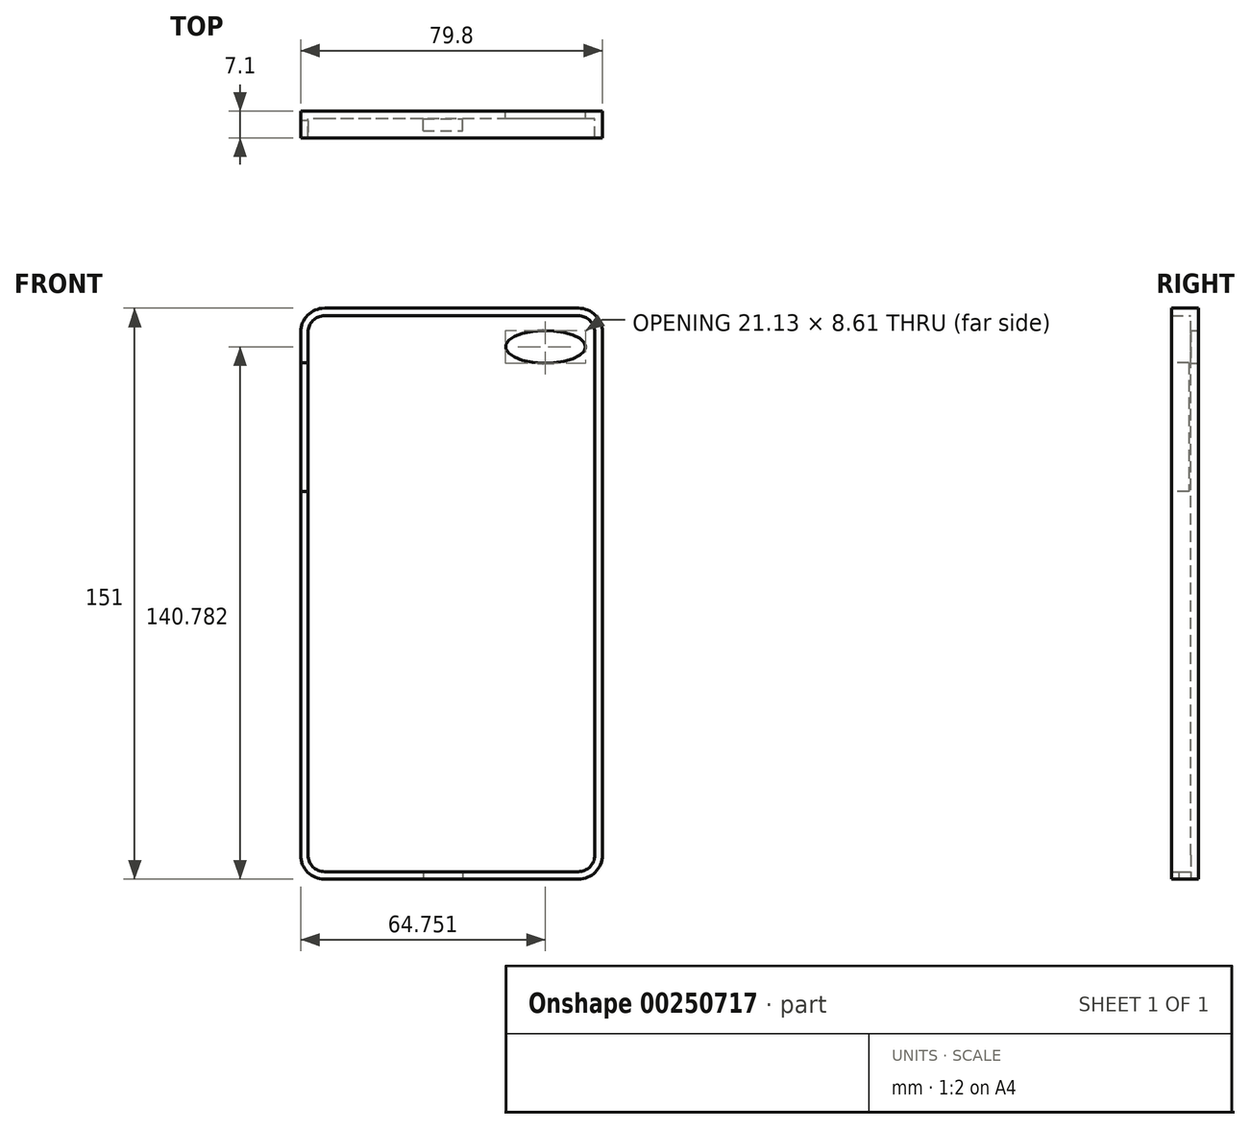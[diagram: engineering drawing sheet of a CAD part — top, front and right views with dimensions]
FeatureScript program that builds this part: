
annotation { "Feature Type Name" : "Feature", "Feature Type Description" : "" }
export const myFeature = defineFeature(function(context is Context, id is Id, definition is map)
    precondition{}
    {
        {
            var Q0;
            Q0=qCreatedBy(makeId("Front.planeOp"),FACE);
            var sketch = newSketch(context, id + "F0", { "sketchPlane" : qUnion([Q0])});
            skLineSegment(sketch, "E0.bottom", {"start": v(35.05, 79.1) * mm, "end": v(-32.05, 79.1) * mm});
            skLineSegment(sketch, "E0.top", {"start": v(35.05, -71.9) * mm, "end": v(-32.05, -71.9) * mm});
            skLineSegment(sketch, "E0.left", {"start": v(-38.4, -65.56) * mm, "end": v(-38.4, 72.74) * mm});
            skLineSegment(sketch, "E0.right", {"start": v(41.4, -65.56) * mm, "end": v(41.4, 72.74) * mm});
            skPoint(sketch, "E0.middle", {"position": v(1.5, 3.6) * mm});
            skLineSegment(sketch, "E1.bottom", {"start": v(27.8, -50.28) * mm, "end": v(-24, -50.28) * mm});
            skLineSegment(sketch, "E1.top", {"start": v(27.8, 61.47) * mm, "end": v(-24, 61.47) * mm});
            skLineSegment(sketch, "E1.left", {"start": v(27.8, -50.28) * mm, "end": v(27.8, 61.47) * mm});
            skLineSegment(sketch, "E1.right", {"start": v(-24, -50.28) * mm, "end": v(-24, 61.47) * mm});
            skPoint(sketch, "E2.visualSharp", {"position": v(-38.4, 79.1) * mm});
            skArc(sketch, "E2.filletArc", {"start": v(-32.05, 79.1) * mm, "mid": v(-36.54, 77.23) * mm, "end": v(-38.4, 72.74) * mm});
            skArc(sketch, "E3.filletArc", {"start": v(41.4, 72.74) * mm, "mid": v(39.54, 77.23) * mm, "end": v(35.05, 79.1) * mm});
            skArc(sketch, "E4.filletArc", {"start": v(35.05, -71.9) * mm, "mid": v(39.54, -70.05) * mm, "end": v(41.4, -65.56) * mm});
            skArc(sketch, "E5.filletArc", {"start": v(-38.4, -65.56) * mm, "mid": v(-36.54, -70.05) * mm, "end": v(-32.05, -71.9) * mm});
            skPoint(sketch, "E6.first.point", {"position": v(-12.34, 73.79) * mm});
            skPoint(sketch, "E6.second.point", {"position": v(-23.23, 68.34) * mm});
            skPoint(sketch, "E6.third.point", {"position": v(-21.29, 65.62) * mm});
            skSolve(sketch);
        }
        {
            var Q0;
            Q0=makeQuery(id+"F0.imprint","IMPRINT",FACE,{"disambiguationData":[TD([[makeQuery(id+"F0.imprint","IMPRINT",EDGE,{"derivedFrom":sQuery(id+"F0.wireOp",EDGE,"E1.bottom")}),-1.0]])]});
            var Q1;
            Q1=makeQuery(id+"F0.imprint","IMPRINT",FACE,{"disambiguationData":[TD([[makeQuery(id+"F0.imprint","IMPRINT",EDGE,{"derivedFrom":sQuery(id+"F0.wireOp",EDGE,"E0.bottom")}),1.0]])]});
            extrude(context, id + "F1", {"entities" : qUnion([Q0, Q1]), "endBound" : BoundingType.SYMMETRIC, "depth" : 7.1 * mm});
        }
        {
            var Q0;
            Q0=makeQuery(id+"F1.opExtrude","CAP_FACE",FACE,{"disambiguationData":[OSD([sQuery(id+"F0.wireOp",EDGE,"E0.bottom"),sQuery(id+"F0.wireOp",EDGE,"E0.top"),sQuery(id+"F0.wireOp",EDGE,"E0.left"),sQuery(id+"F0.wireOp",EDGE,"E0.right"),sQuery(id+"F0.wireOp",EDGE,"E2.filletArc"),sQuery(id+"F0.wireOp",EDGE,"E3.filletArc"),sQuery(id+"F0.wireOp",EDGE,"E4.filletArc"),sQuery(id+"F0.wireOp",EDGE,"E5.filletArc"),sQuery(id+"F0.wireOp",EDGE,"bcc29a37-80d4-4e82-a1c9-099fcf55504c")])],"isStart":false});
            shell(context, id + "F2", {"entities" : qUnion([Q0]), "thickness" : 2 * mm});
        }
        {
            var Q0;
            Q0=makeQuery(id+"F1.opExtrude","SWEPT_FACE",FACE,{"disambiguationData":[OSD([sQuery(id+"F0.wireOp",EDGE,"E0.top")])]});
            var sketch = newSketch(context, id + "F3", { "sketchPlane" : qUnion([Q0])});
            skLineSegment(sketch, "E7.bottom", {"start": v(-6.02, 1.68) * mm, "end": v(4.5, 1.68) * mm});
            skLineSegment(sketch, "E7.top", {"start": v(-6.02, -1.56) * mm, "end": v(4.5, -1.56) * mm});
            skLineSegment(sketch, "E7.left", {"start": v(-6.02, 1.68) * mm, "end": v(-6.02, -1.56) * mm});
            skLineSegment(sketch, "E7.right", {"start": v(4.5, 1.68) * mm, "end": v(4.5, -1.56) * mm});
            skSolve(sketch);
        }
        {
            var Q0;
            Q0=makeQuery(id+"F3.imprint","IMPRINT",FACE,{"disambiguationData":[TD([[makeQuery(id+"F3.imprint","IMPRINT",EDGE,{"derivedFrom":sQuery(id+"F3.wireOp",EDGE,"E7.bottom")}),-1.0]])]});
            extrude(context, id + "F4", {"entities" : qUnion([Q0]), "operationType" : NewBodyOperationType.REMOVE, "oppositeDirection" : true, "depth" : 25 * mm});
        }
        {
            var Q0;
            Q0=makeQuery(id+"F1.opExtrude","CAP_FACE",FACE,{"disambiguationData":[OSD([sQuery(id+"F0.wireOp",EDGE,"E0.bottom"),sQuery(id+"F0.wireOp",EDGE,"E0.top"),sQuery(id+"F0.wireOp",EDGE,"E0.left"),sQuery(id+"F0.wireOp",EDGE,"E0.right"),sQuery(id+"F0.wireOp",EDGE,"E2.filletArc"),sQuery(id+"F0.wireOp",EDGE,"E3.filletArc"),sQuery(id+"F0.wireOp",EDGE,"E4.filletArc"),sQuery(id+"F0.wireOp",EDGE,"E5.filletArc")])],"isStart":true});
            var sketch = newSketch(context, id + "F5", { "sketchPlane" : qUnion([Q0])});
            skEllipse(sketch, "E8", {"center": v(-26.35, 68.87) * mm, "majorRadius": 10.57 * mm, "minorRadius": 4.3 * mm, "majorAxis": v(-1, 0)});
            skSolve(sketch);
        }
        {
            var Q0;
            Q0=makeQuery(id+"F5.imprint","IMPRINT",FACE,{"disambiguationData":[TD([[makeQuery(id+"F5.imprint","IMPRINT",EDGE,{"derivedFrom":sQuery(id+"F5.wireOp",EDGE,"E8")}),1.0]])]});
            extrude(context, id + "F6", {"entities" : qUnion([Q0]), "operationType" : NewBodyOperationType.REMOVE, "oppositeDirection" : true, "depth" : 25 * mm});
        }
        {
            var Q0;
            Q0=makeQuery(id+"F1.opExtrude","SWEPT_FACE",FACE,{"disambiguationData":[OSD([sQuery(id+"F0.wireOp",EDGE,"E0.left")])]});
            var sketch = newSketch(context, id + "F7", { "sketchPlane" : qUnion([Q0])});
            skLineSegment(sketch, "E9.bottom", {"start": v(-1.02, 64.68) * mm, "end": v(3.55, 64.68) * mm});
            skLineSegment(sketch, "E9.top", {"start": v(-1.02, 30.68) * mm, "end": v(3.55, 30.68) * mm});
            skLineSegment(sketch, "E9.left", {"start": v(-1.02, 64.68) * mm, "end": v(-1.02, 30.68) * mm});
            skLineSegment(sketch, "E9.right", {"start": v(3.55, 64.68) * mm, "end": v(3.55, 30.68) * mm});
            skSolve(sketch);
        }
        {
            var Q0;
            Q0 = qSketchRegion(id + "F7", true);
            extrude(context, id + "F8", {"entities" : qUnion([Q0]), "operationType" : NewBodyOperationType.REMOVE, "oppositeDirection" : true, "depth" : 25 * mm});
        }
    });
